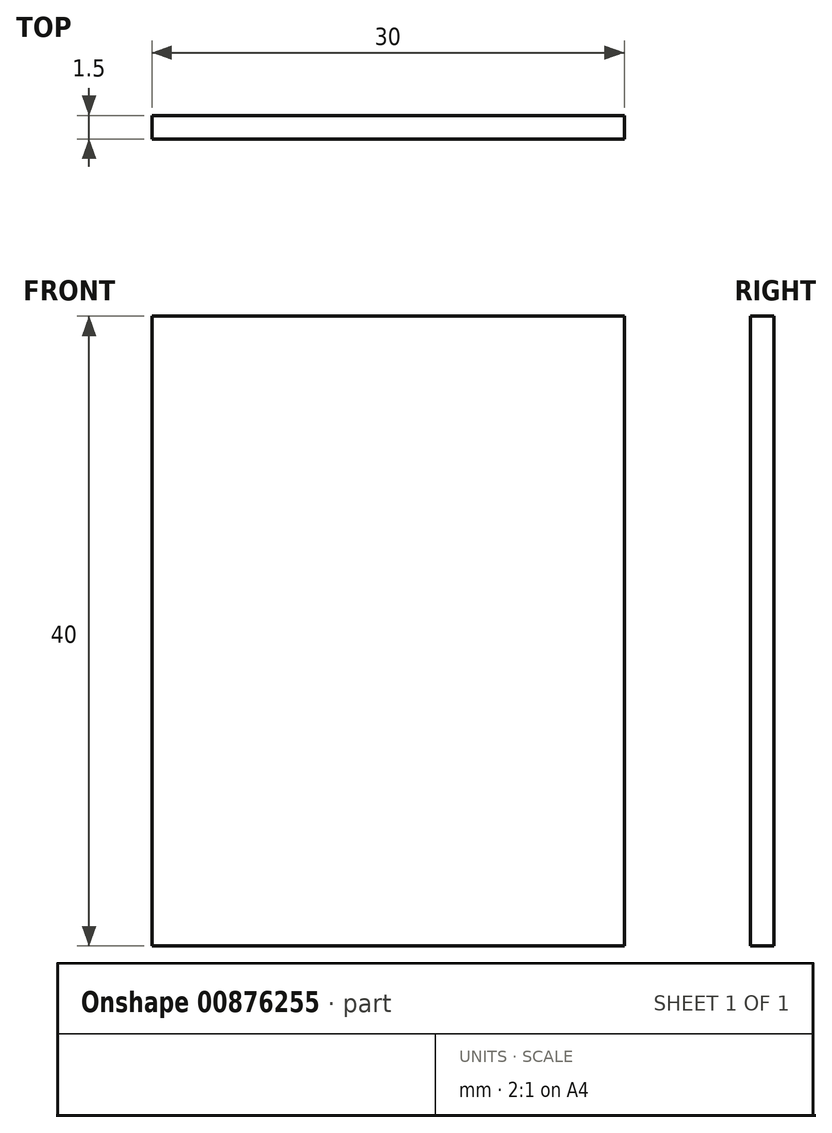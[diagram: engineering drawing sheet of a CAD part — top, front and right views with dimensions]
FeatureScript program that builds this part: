
annotation { "Feature Type Name" : "Feature", "Feature Type Description" : "" }
export const myFeature = defineFeature(function(context is Context, id is Id, definition is map)
    precondition{}
    {
        {
            var Q0;
            Q0=qCreatedBy(makeId("Front.planeOp"),FACE);
            var sketch = newSketch(context, id + "F0", { "sketchPlane" : qUnion([Q0])});
            skLineSegment(sketch, "E0.bottom", {"start": v(2.81, 0) * mm, "end": v(32.81, 0) * mm});
            skLineSegment(sketch, "E0.top", {"start": v(2.81, -40) * mm, "end": v(32.81, -40) * mm});
            skLineSegment(sketch, "E0.left", {"start": v(2.81, 0) * mm, "end": v(2.81, -40) * mm});
            skLineSegment(sketch, "E0.right", {"start": v(32.81, 0) * mm, "end": v(32.81, -40) * mm});
            skSolve(sketch);
        }
        {
            var Q0;
            Q0=makeQuery(id+"F0.imprint","IMPRINT",FACE,{"disambiguationData":[TD([[makeQuery(id+"F0.imprint","IMPRINT",EDGE,{"derivedFrom":sQuery(id+"F0.wireOp",EDGE,"E0.bottom")}),-1.0]])]});
            extrude(context, id + "F1", {"entities" : qUnion([Q0]), "depth" : 1.5 * mm, "offsetDistance" : 25.4 * mm});
        }
    });
